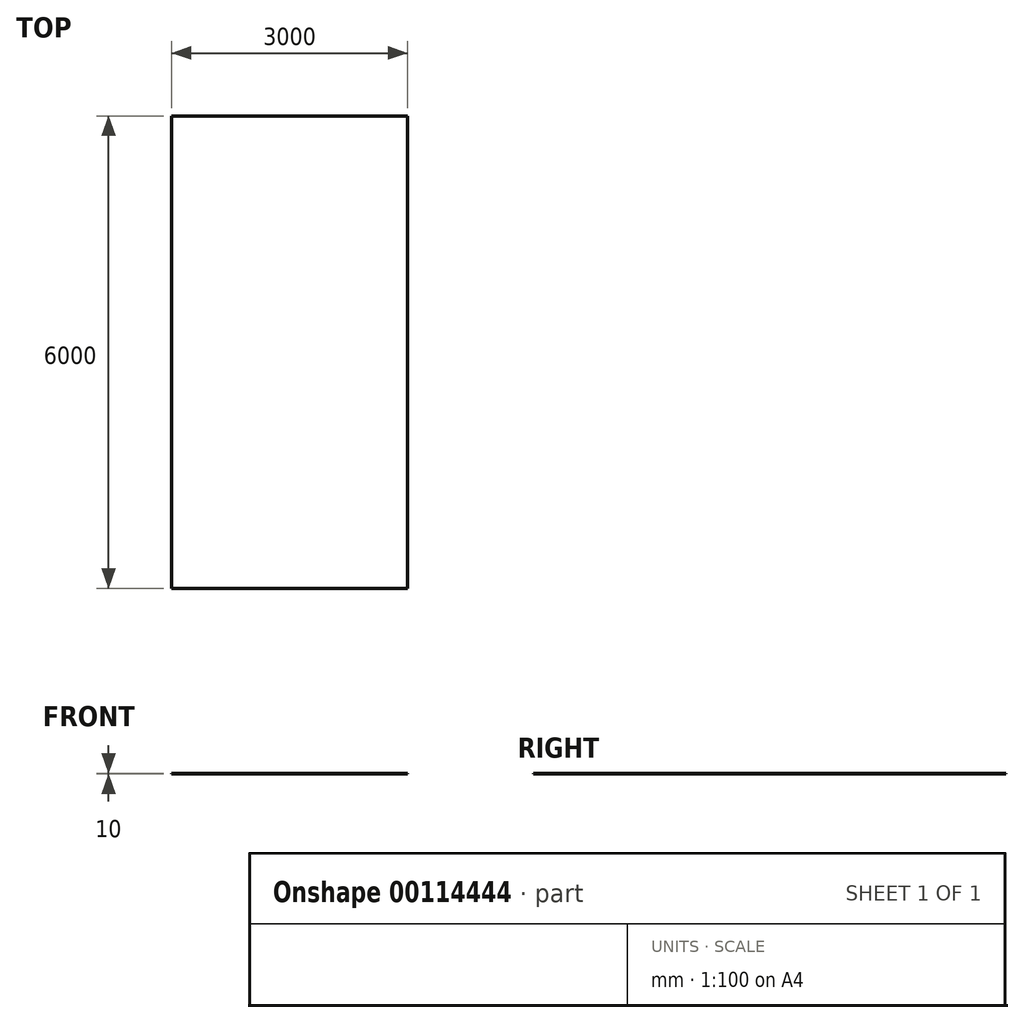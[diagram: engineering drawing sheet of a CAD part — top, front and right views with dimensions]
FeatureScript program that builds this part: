
annotation { "Feature Type Name" : "Feature", "Feature Type Description" : "" }
export const myFeature = defineFeature(function(context is Context, id is Id, definition is map)
    precondition{}
    {
        {
            var Q0;
            Q0=qCreatedBy(makeId("Top.planeOp"),FACE);
            var sketch = newSketch(context, id + "F0", { "sketchPlane" : qUnion([Q0])});
            skLineSegment(sketch, "E0.bottom", {"start": v(1500, -3000) * mm, "end": v(-1500, -3000) * mm});
            skLineSegment(sketch, "E0.top", {"start": v(1500, 3000) * mm, "end": v(-1500, 3000) * mm});
            skLineSegment(sketch, "E0.left", {"start": v(1500, -3000) * mm, "end": v(1500, 3000) * mm});
            skLineSegment(sketch, "E0.right", {"start": v(-1500, -3000) * mm, "end": v(-1500, 3000) * mm});
            skPoint(sketch, "E0.middle", {"position": v(0, 0) * mm});
            skSolve(sketch);
        }
        {
            var Q0;
            Q0 = qSketchRegion(id + "F0", true);
            extrude(context, id + "F1", {"entities" : qUnion([Q0]), "depth" : 10 * mm});
        }
    });
